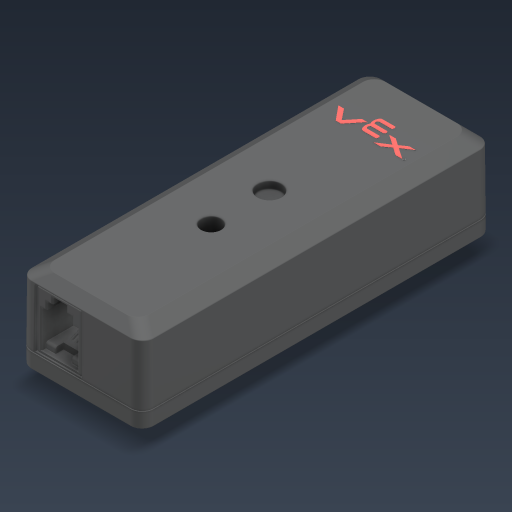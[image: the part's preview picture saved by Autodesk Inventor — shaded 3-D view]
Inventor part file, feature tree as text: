
AUTODESK INVENTOR PART (.ipt)
format: ipt  version: 2023 (Build 270158000, 158)  size: 5,428,736 bytes
history: native  units: in
note: dims shown in document units (in); Inventor stores cm internally (conversion verified against a paired STEP export)
features: other x7, extrude x1, sketch x1
ambient origin geometry x8: Origin, YZ Plane, XZ Plane, XY Plane, X Axis, Y Axis, Z Axis, Center Point
bodies: Solid1 (feature_tree), Solid2 (feature_tree), Solid3 (feature_tree), Solid4 (feature_tree), Solid5 (feature_tree), Solid6 (feature_tree)
feature tree (9):
  other  "V5 3-Wire Expander (276-5299).iam"
  other  "276-5299-010 Web.ipt:1"
  other  "276-5299-011 Web.ipt:1"
  other  "276-5299-012 Web.ipt:1"
  other  "276-5299-013 Web.ipt:1"
  other  "276-5299-900 Web.iam:1::V5 Connector Web.ipt:1"
  other  "276-5299-900 Web.iam:1::3-Wire Connector Web.ipt:1"
  extrude  "Extrusion1"  Depth=0.3937in TaperAngle=0.0deg
  sketch  "Sketch1"  dims[d0=0.3937in d16=0.002in d17=0.0in]
